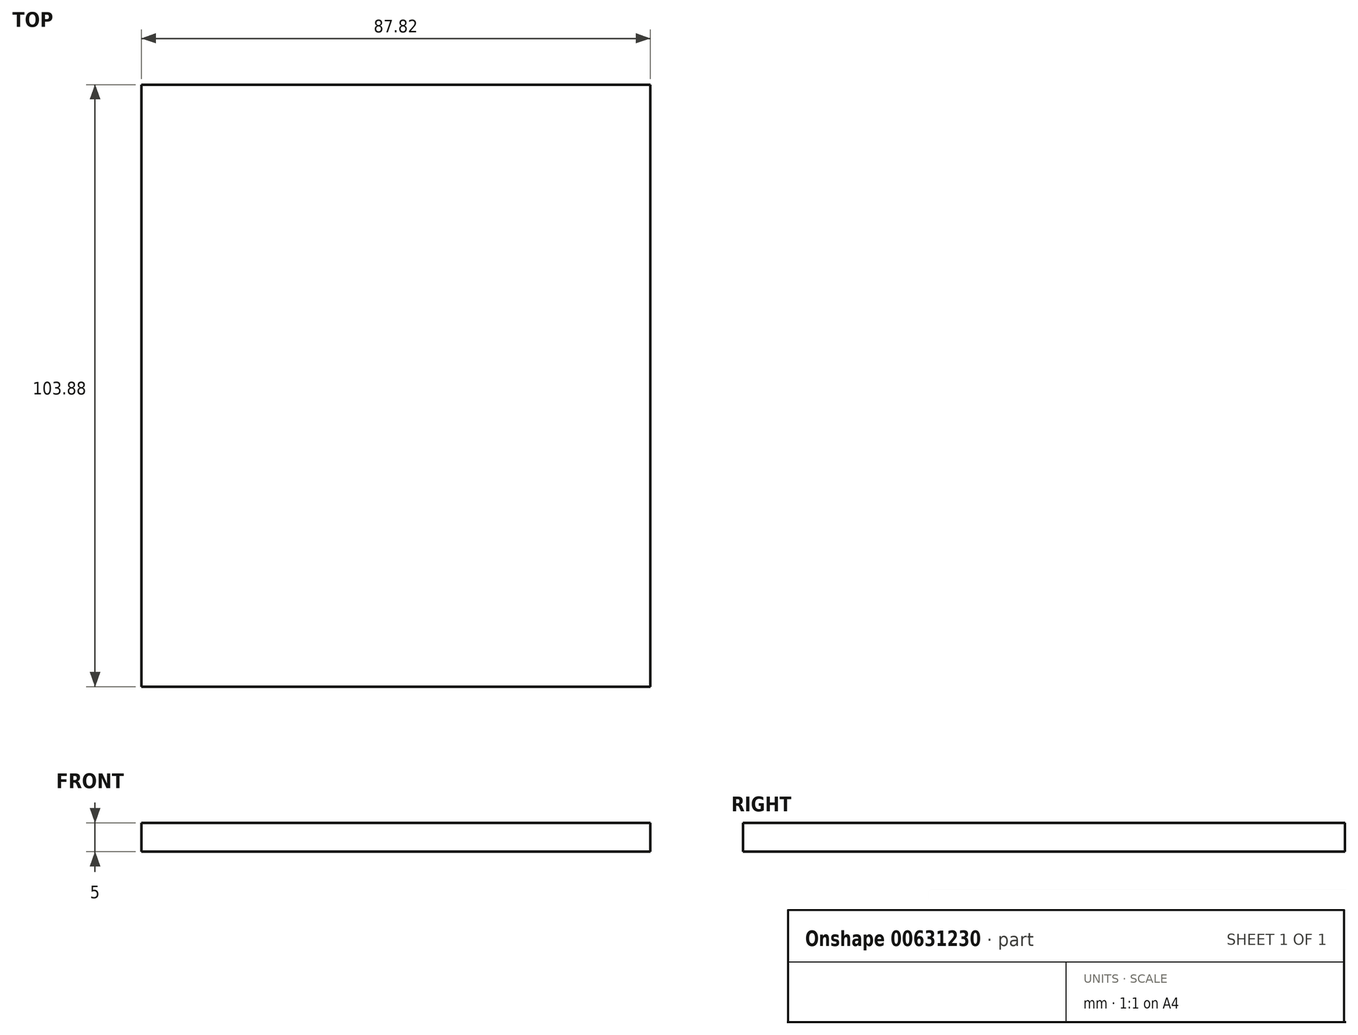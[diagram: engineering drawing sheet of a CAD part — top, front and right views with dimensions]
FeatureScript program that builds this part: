
annotation { "Feature Type Name" : "Feature", "Feature Type Description" : "" }
export const myFeature = defineFeature(function(context is Context, id is Id, definition is map)
    precondition{}
    {
        {
            var Q0;
            Q0=qCreatedBy(makeId("Top.planeOp"),FACE);
            var sketch = newSketch(context, id + "F0", { "sketchPlane" : qUnion([Q0])});
            skLineSegment(sketch, "E0.bottom", {"start": v(43.91, 51.94) * mm, "end": v(-43.91, 51.94) * mm});
            skLineSegment(sketch, "E0.top", {"start": v(43.91, -51.94) * mm, "end": v(-43.91, -51.94) * mm});
            skLineSegment(sketch, "E0.left", {"start": v(43.91, 51.94) * mm, "end": v(43.91, -51.94) * mm});
            skLineSegment(sketch, "E0.right", {"start": v(-43.91, 51.94) * mm, "end": v(-43.91, -51.94) * mm});
            skPoint(sketch, "E0.middle", {"position": v(0, 0) * mm});
            skLineSegment(sketch, "E1.top", {"start": v(43.91, -30.98) * mm, "end": v(-43.91, -30.98) * mm});
            skLineSegment(sketch, "E1.left", {"start": v(43.91, -51.94) * mm, "end": v(43.91, -30.98) * mm});
            skLineSegment(sketch, "E1.right", {"start": v(-43.91, -51.94) * mm, "end": v(-43.91, -30.98) * mm});
            skSolve(sketch);
        }
        {
            var Q0;
            Q0=makeQuery(id+"F0.imprint","IMPRINT",FACE,{"disambiguationData":[TD([[makeQuery(id+"F0.imprint","IMPRINT",EDGE,{"derivedFrom":sQuery(id+"F0.wireOp",EDGE,"E0.bottom")}),1.0]])]});
            var Q1;
            Q1=makeQuery(id+"F0.imprint","IMPRINT",FACE,{"disambiguationData":[TD([[makeQuery(id+"F0.imprint","IMPRINT",EDGE,{"derivedFrom":sQuery(id+"F0.wireOp",EDGE,"E0.top")}),-1.0]])]});
            extrude(context, id + "F1", {"entities" : qUnion([Q0, Q1]), "oppositeDirection" : true, "depth" : 5 * mm, "offsetDistance" : 25 * mm});
        }
    });
